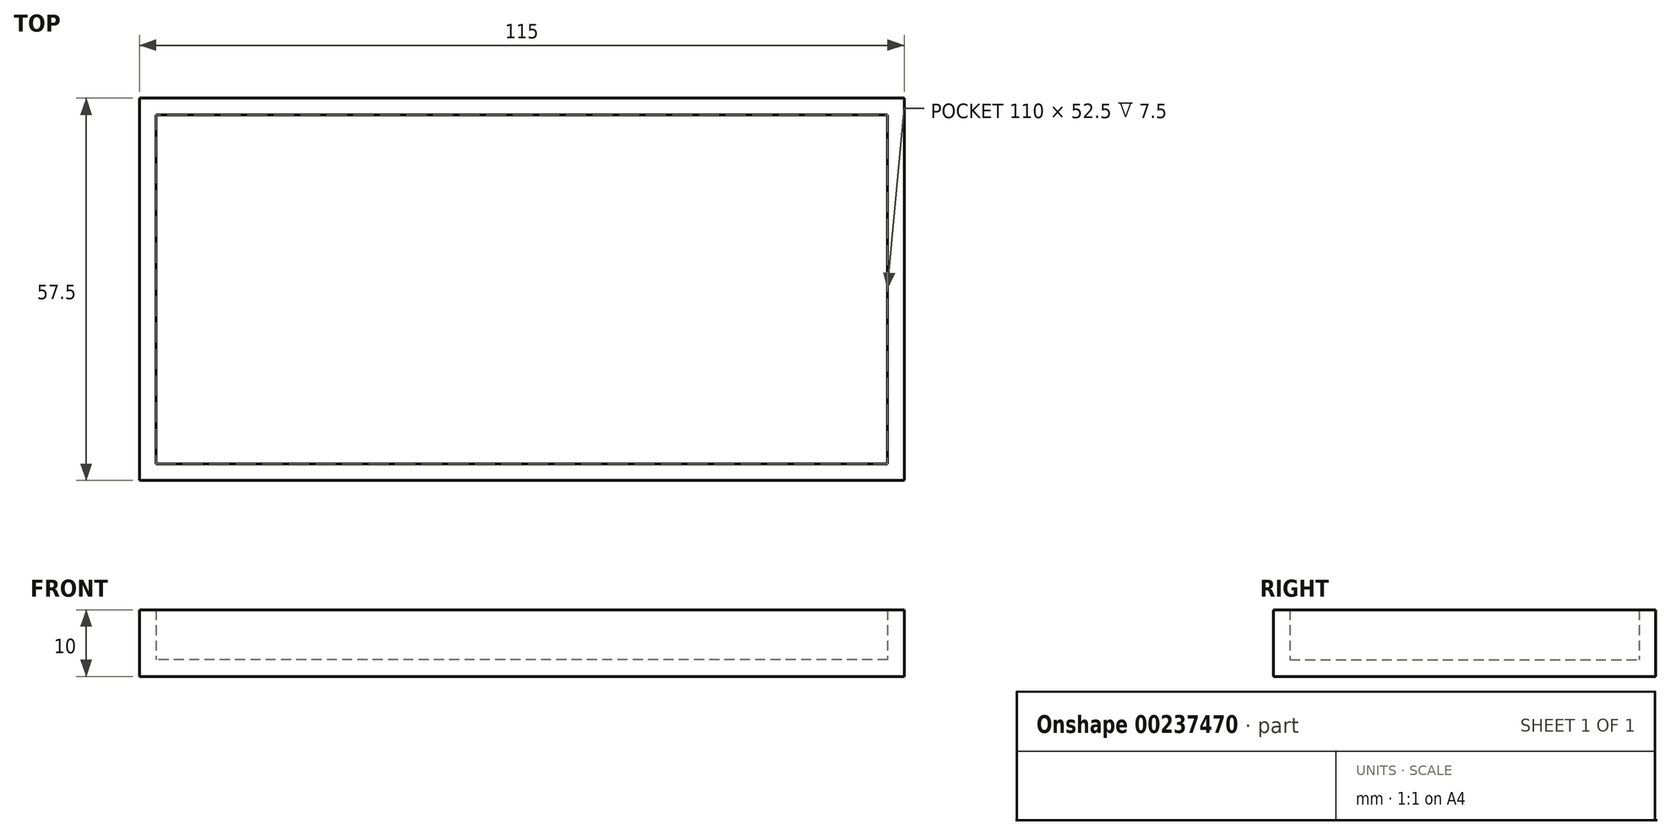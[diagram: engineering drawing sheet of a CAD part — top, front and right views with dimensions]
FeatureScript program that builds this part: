
annotation { "Feature Type Name" : "Feature", "Feature Type Description" : "" }
export const myFeature = defineFeature(function(context is Context, id is Id, definition is map)
    precondition{}
    {
        {
            var Q0;
            Q0=qCreatedBy(makeId("Top.planeOp"),FACE);
            var sketch = newSketch(context, id + "F0", { "sketchPlane" : qUnion([Q0])});
            skLineSegment(sketch, "E0.bottom", {"start": v(0, 0) * mm, "end": v(-115, 0) * mm});
            skLineSegment(sketch, "E0.top", {"start": v(0, 57.5) * mm, "end": v(-115, 57.5) * mm});
            skLineSegment(sketch, "E0.left", {"start": v(0, 0) * mm, "end": v(0, 57.5) * mm});
            skLineSegment(sketch, "E0.right", {"start": v(-115, 0) * mm, "end": v(-115, 57.5) * mm});
            skSolve(sketch);
        }
        {
            var Q0;
            Q0=makeQuery(id+"F0.imprint","IMPRINT",FACE,{"disambiguationData":[TD([[makeQuery(id+"F0.imprint","IMPRINT",EDGE,{"derivedFrom":sQuery(id+"F0.wireOp",EDGE,"E0.bottom")}),-1.0]])]});
            extrude(context, id + "F1", {"entities" : qUnion([Q0]), "depth" : 10 * mm});
        }
        {
            var Q0;
            Q0=makeQuery(id+"F1.opExtrude","CAP_FACE",FACE,{"disambiguationData":[OSD([sQuery(id+"F0.wireOp",EDGE,"E0.bottom"),sQuery(id+"F0.wireOp",EDGE,"E0.top"),sQuery(id+"F0.wireOp",EDGE,"E0.left"),sQuery(id+"F0.wireOp",EDGE,"E0.right")])],"isStart":false});
            var Q1;
            Q1=makeQuery(id+"F1.opExtrude","SWEPT_BODY",BODY,{"disambiguationData":[OSD([sQuery(id+"F0.wireOp",EDGE,"E0.bottom"),sQuery(id+"F0.wireOp",EDGE,"E0.top"),sQuery(id+"F0.wireOp",EDGE,"E0.left"),sQuery(id+"F0.wireOp",EDGE,"E0.right")])]});
            shell(context, id + "F2", {"entities" : qUnion([Q0]), "parts" : qUnion([Q1]), "thickness" : 2.5 * mm});
        }
    });
